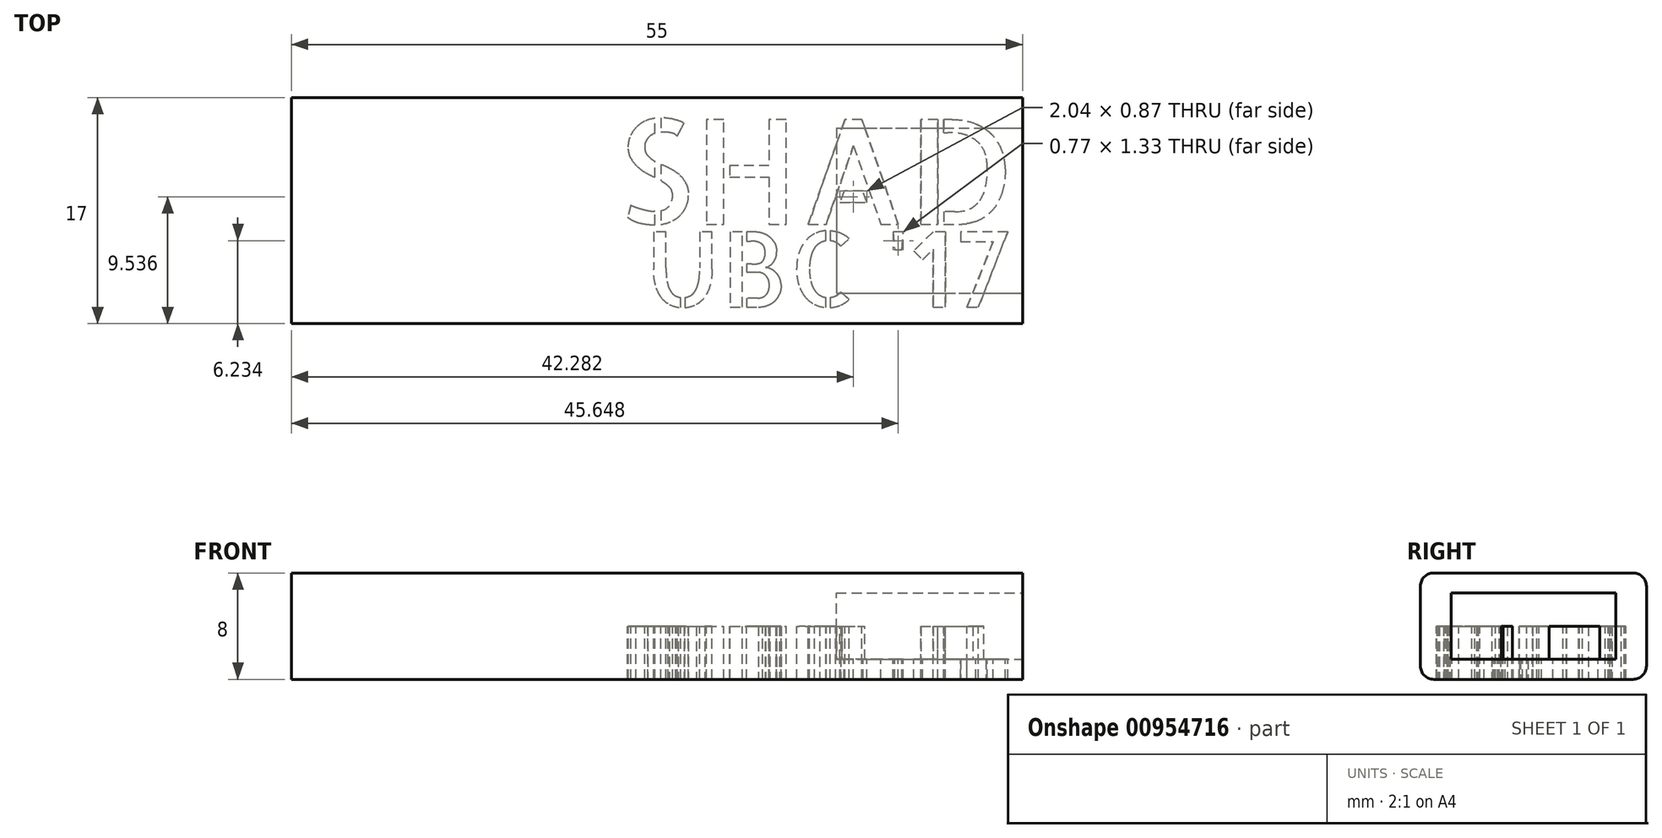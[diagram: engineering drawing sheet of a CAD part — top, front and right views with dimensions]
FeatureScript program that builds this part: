
annotation { "Feature Type Name" : "Feature", "Feature Type Description" : "" }
export const myFeature = defineFeature(function(context is Context, id is Id, definition is map)
    precondition{}
    {
        {
            var Q0;
            Q0=qCreatedBy(makeId("Front.planeOp"),FACE);
            var sketch = newSketch(context, id + "F0", { "sketchPlane" : qUnion([Q0])});
            skLineSegment(sketch, "E0.bottom", {"start": v(7.5, -4) * mm, "end": v(-7.5, -4) * mm});
            skLineSegment(sketch, "E0.top", {"start": v(7.5, 4) * mm, "end": v(-7.5, 4) * mm});
            skLineSegment(sketch, "E0.left", {"start": v(8.5, -3) * mm, "end": v(8.5, 3) * mm});
            skLineSegment(sketch, "E0.right", {"start": v(-8.5, -3) * mm, "end": v(-8.5, 3) * mm});
            skPoint(sketch, "E0.middle", {"position": v(0, 0) * mm});
            skPoint(sketch, "E1.visualSharp", {"position": v(-8.5, 4) * mm});
            skArc(sketch, "E1.filletArc", {"start": v(-7.5, 4) * mm, "mid": v(-8.2, 3.7) * mm, "end": v(-8.5, 3) * mm});
            skPoint(sketch, "E2.visualSharp", {"position": v(-8.5, -4) * mm});
            skArc(sketch, "E2.filletArc", {"start": v(-8.5, -3) * mm, "mid": v(-8.2, -3.7) * mm, "end": v(-7.5, -4) * mm});
            skPoint(sketch, "E3.visualSharp", {"position": v(8.5, -4) * mm});
            skArc(sketch, "E3.filletArc", {"start": v(7.5, -4) * mm, "mid": v(8.2, -3.7) * mm, "end": v(8.5, -3) * mm});
            skPoint(sketch, "E4.visualSharp", {"position": v(8.5, 4) * mm});
            skArc(sketch, "E4.filletArc", {"start": v(8.5, 3) * mm, "mid": v(8.2, 3.7) * mm, "end": v(7.5, 4) * mm});
            skSolve(sketch);
        }
        {
            var Q0;
            Q0=qSketchRegion(id+"F0",true);
            extrude(context, id + "F1", {"entities" : qUnion([Q0]), "depth" : 55 * mm, "offsetDistance" : 25 * mm});
        }
        {
            var Q0;
            Q0=makeQuery(id+"F1.opExtrude","CAP_FACE",FACE,{"disambiguationData":[OSD([sQuery(id+"F0.wireOp",EDGE,"E0.bottom"),sQuery(id+"F0.wireOp",EDGE,"E0.top"),sQuery(id+"F0.wireOp",EDGE,"E0.left"),sQuery(id+"F0.wireOp",EDGE,"E0.right"),sQuery(id+"F0.wireOp",EDGE,"E1.filletArc"),sQuery(id+"F0.wireOp",EDGE,"E2.filletArc"),sQuery(id+"F0.wireOp",EDGE,"E3.filletArc"),sQuery(id+"F0.wireOp",EDGE,"E4.filletArc")])],"isStart":false});
            var sketch = newSketch(context, id + "F2", { "sketchPlane" : qUnion([Q0])});
            skLineSegment(sketch, "E5.bottom", {"start": v(6.2, -2.5) * mm, "end": v(-6.2, -2.5) * mm});
            skLineSegment(sketch, "E5.top", {"start": v(6.2, 2.5) * mm, "end": v(-6.2, 2.5) * mm});
            skLineSegment(sketch, "E5.left", {"start": v(6.2, -2.5) * mm, "end": v(6.2, 2.5) * mm});
            skLineSegment(sketch, "E5.right", {"start": v(-6.2, -2.5) * mm, "end": v(-6.2, 2.5) * mm});
            skPoint(sketch, "E5.middle", {"position": v(0, 0) * mm});
            skSolve(sketch);
        }
        {
            var Q0;
            Q0=makeQuery(id+"F2.imprint","IMPRINT",FACE,{"disambiguationData":[TD([[makeQuery(id+"F2.imprint","IMPRINT",EDGE,{"derivedFrom":sQuery(id+"F2.wireOp",EDGE,"E5.bottom")}),-1.0]])]});
            extrude(context, id + "F3", {"entities" : qUnion([Q0]), "operationType" : NewBodyOperationType.REMOVE, "oppositeDirection" : true, "depth" : 14 * mm, "offsetDistance" : 25 * mm});
        }
        {
            var Q0;
            Q0=makeQuery(id+"F1.opExtrude","SWEPT_BODY",BODY,{"disambiguationData":[OSD([sQuery(id+"F0.wireOp",EDGE,"E0.bottom"),sQuery(id+"F0.wireOp",EDGE,"E0.top"),sQuery(id+"F0.wireOp",EDGE,"E0.left"),sQuery(id+"F0.wireOp",EDGE,"E0.right"),sQuery(id+"F0.wireOp",EDGE,"E1.filletArc"),sQuery(id+"F0.wireOp",EDGE,"E2.filletArc"),sQuery(id+"F0.wireOp",EDGE,"E3.filletArc"),sQuery(id+"F0.wireOp",EDGE,"E4.filletArc")])]});
            var Q1;
            Q1=makeQuery(id+"F1.opExtrude","CAP_EDGE",EDGE,{"disambiguationData":[OSD([sQuery(id+"F0.wireOp",EDGE,"E0.left")])],"isStart":true});
            transform(context, id + "F4", {"entities" : qUnion([Q0]), "transformType" : TransformType.ROTATION, "transformAxis" : qUnion([Q1]), "angle" : 90 * degree, "makeCopy" : false});
        }
        {
            var Q0;
            Q0=qCreatedBy(makeId("Top.planeOp"),FACE);
            var sketch = newSketch(context, id + "F5", { "sketchPlane" : qUnion([Q0])});
            skText(sketch, "E6", { "text": "SHAD", "fontName": "AllertaStencil-Regular.ttf"});
            const initialGuessF5  = {"E6": [0.03294, -0.00953, 1, 0, 0.00787]};
            skSetInitialGuess(sketch, initialGuessF5);
            skSolve(sketch);
        }
        {
            var Q0;
            Q0=qCreatedBy(makeId("Top.planeOp"),FACE);
            var sketch = newSketch(context, id + "F6", { "sketchPlane" : qUnion([Q0])});
            skText(sketch, "E7", { "text": "UBC \'17", "fontName": "AllertaStencil-Regular.ttf"});
            const initialGuessF6  = {"E7": [0.03512, -0.01576, 1, 0, 0.00566]};
            skSetInitialGuess(sketch, initialGuessF6);
            skSolve(sketch);
        }
        {
            var Q0;
            Q0 = qSketchRegion(id + "F6", true);
            var Q1;
            Q1 = qSketchRegion(id + "F5", true);
            extrude(context, id + "F7", {"entities" : qUnion([Q0, Q1]), "operationType" : NewBodyOperationType.REMOVE, "oppositeDirection" : true, "depth" : 75 * mm, "offsetDistance" : 25 * mm});
        }
    });
